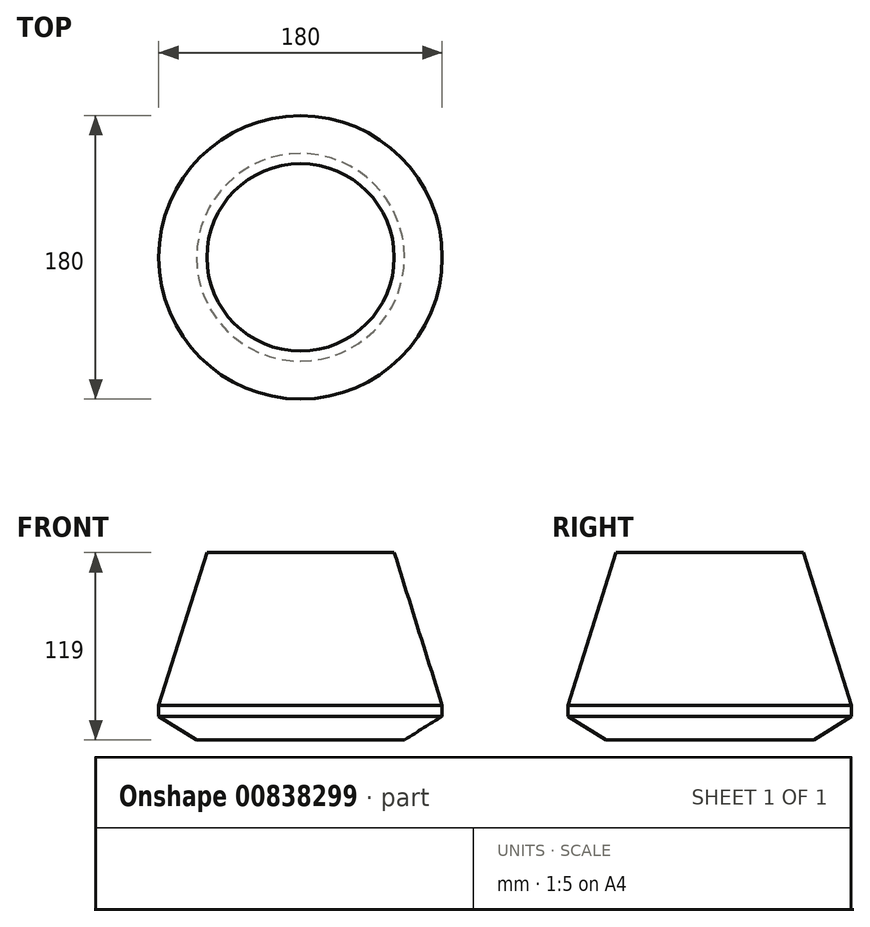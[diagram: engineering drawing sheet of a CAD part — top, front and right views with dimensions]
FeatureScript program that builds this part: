
annotation { "Feature Type Name" : "Feature", "Feature Type Description" : "" }
export const myFeature = defineFeature(function(context is Context, id is Id, definition is map)
    precondition{}
    {
        {
            var Q0;
            Q0=qCreatedBy(makeId("Front.planeOp"),FACE);
            var sketch = newSketch(context, id + "F0", { "sketchPlane" : qUnion([Q0])});
            skLineSegment(sketch, "E0", {"start": v(0, 59.5) * mm, "end": v(0, -59.5) * mm});
            skLineSegment(sketch, "E1", {"start": v(0, -59.5) * mm, "end": v(-66, -59.5) * mm});
            skLineSegment(sketch, "E2", {"start": v(-66, -59.5) * mm, "end": v(-90, -44.5) * mm});
            skLineSegment(sketch, "E3", {"start": v(-90, -44.5) * mm, "end": v(-90, -37.5) * mm});
            skLineSegment(sketch, "E4", {"start": v(-90, -37.5) * mm, "end": v(-59.5, 59.5) * mm});
            skLineSegment(sketch, "E5", {"start": v(-59.5, 59.5) * mm, "end": v(0, 59.5) * mm});
            skSolve(sketch);
        }
        {
            var Q0;
            Q0=makeQuery(id+"F0.imprint","IMPRINT",FACE,{"disambiguationData":[TD([[makeQuery(id+"F0.imprint","IMPRINT",EDGE,{"derivedFrom":sQuery(id+"F0.wireOp",EDGE,"E0")}),-1.0]])]});
            var Q1;
            Q1=sQuery(id+"F0.wireOp",EDGE,"E0");
            revolve(context, id + "F1", {"surfaceOperationType" : NewSurfaceOperationType.NEW, "entities" : qUnion([Q0]), "axis" : qUnion([Q1]), "revolveType" : RevolveType.FULL});
        }
    });
